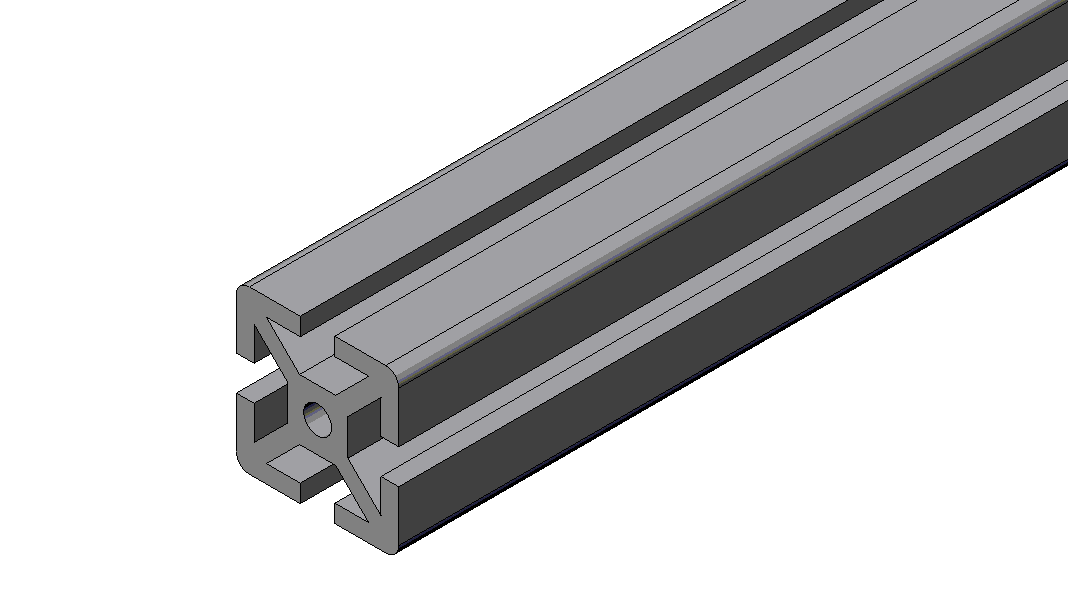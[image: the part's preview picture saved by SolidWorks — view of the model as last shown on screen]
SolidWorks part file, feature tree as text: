
SOLIDWORKS PART (.sldprt)
format: sldprt  version: not decoded by parser v0  size: 2,478,592 bytes
history: native  units: mm
features: sketch x48, cut_extrude x47, material x1 (+38 scaffold rows collapsed; 12 parser-record rows omitted)
feature tree (146):
  scaffold x38  (default folders/planes/origin — collapsed)
  material  "Material <not specified>"
  parser-record x12  (decoder bookkeeping rows leaked as tree rows — omitted from the tree; the rows remain in map.json)
  sketch  "Sketch1"  dims[c1.D2=3.048mm c1.D5=1.016mm c1.D6=1.016mm c1.D13=~1.042776mm c1.D15=6.5278mm c1.D3=5.08mm c1.D1=~17.549308mm c2.D1=45.0deg c2.D3=4.826mm c2.D4=4.826mm c2.D7=7.62mm c2.D8=7.62mm c2.D9=19.05mm c2.D10=12.7mm c2.D11=~7.529984mm c3.D11=2.0deg c3.D12=~36.763158mm c4.D12=3.0deg c5.D12=~36.763158mm c6.D12=2.0deg c6.D14=3.302mm c6.D10=19.05mm c6.D3=4.826mm c6.D5=4.064mm c6.D6=3.2385mm c6.D7=3.2385mm c6.D8=7.7724mm c6.D11=7.7724mm c7.D3=11.938mm c7.D4=11.938mm c7.D6=14.986mm c7.D7=9.4742mm]
  cut_extrude  "FinalCut"  Depth=609.6mm CutLength=609.6mm
  sketch  "Sketch38"
  sketch  "Sketch3"  dims[D1=20.6248mm D2=21.717mm]
  cut_extrude  "AFA1"  Depth=16.51mm
  sketch  "Sketch5"  dims[D1=20.6248mm D2=21.717mm]
  cut_extrude  "AFA2"  Depth=16.51mm
  sketch  "Sketch6"  dims[c1.D1=20.6248mm c1.D2=20.6248mm c2.D1=21.717mm]
  cut_extrude  "AFA3"  Depth=16.51mm
  sketch  "Sketch8"  dims[D2=20.6248mm D1=21.717mm]
  cut_extrude  "AFA4"  Depth=16.51mm
  sketch  "Sketch9"  dims[D2=20.6248mm D1=21.717mm]
  cut_extrude  "AFB1"  Depth=16.51mm
  sketch  "Sketch12"  dims[D2=20.6248mm D1=21.717mm]
  cut_extrude  "AFB2"  Depth=16.51mm
  sketch  "Sketch13"  dims[D3=20.6248mm D1=0.0mm D2=21.717mm]
  cut_extrude  "AFB3"  Depth=16.51mm
  sketch  "Sketch14"  dims[D2=20.6248mm D1=21.717mm]
  cut_extrude  "AFB4"  Depth=16.51mm
  sketch  "Sketch25"  dims[D1=20.6248mm D2=18.3134mm]
  cut_extrude  "BFA1"  Depth=16.51mm
  sketch  "Sketch27"  dims[D1=20.6248mm D2=18.3134mm]
  cut_extrude  "BFA2"  Depth=16.51mm
  sketch  "Sketch24"  dims[c1.D1=20.6248mm c1.D2=20.6248mm c2.D1=18.3134mm]
  cut_extrude  "BFA3"  Depth=16.51mm
  sketch  "Sketch23"  dims[c1.D1=20.6248mm c1.D2=20.6248mm c2.D1=18.3134mm]
  cut_extrude  "BFA4"  Depth=16.51mm
  sketch  "Sketch15"  dims[D2=20.6248mm D1=18.3134mm]
  cut_extrude  "BFB1"  Depth=16.51mm
  sketch  "Sketch17"  dims[D2=20.6248mm D1=18.3134mm]
  cut_extrude  "BFB2"  Depth=16.51mm
  sketch  "Sketch18"  dims[D2=20.6248mm D1=18.3134mm]
  cut_extrude  "BFB3"  Depth=16.51mm
  sketch  "Sketch19"  dims[D2=20.6248mm D1=18.3134mm]
  cut_extrude  "BFB4"  Depth=16.51mm
  sketch  "Sketch28"  dims[D1=7.62mm]
  cut_extrude  "TPA660015"  Depth=25.4mm
  sketch  "Sketch29"  dims[D1=7.62mm]
  cut_extrude  "TPB660015"  Depth=25.4mm
  sketch  "Sketch30"  dims[D1=7.874mm]
  cut_extrude  "TPA660034"  Depth=24.13mm
  sketch  "Sketch31"  dims[D1=7.874mm]
  cut_extrude  "TPB660034"  Depth=24.13mm
  sketch  "Sketch32"  dims[D1=8.128mm]
  cut_extrude  "TPA660033"  Depth=22.86mm
  sketch  "Sketch33"  dims[D1=8.128mm]
  cut_extrude  "TPB660033"  Depth=22.86mm
  sketch  "Sketch34"  dims[D1=9.525mm]
  cut_extrude  "TPA660009"  Depth=21.59mm
  sketch  "Sketch35"  dims[D1=9.525mm]
  cut_extrude  "TPB660009"  Depth=21.59mm
  sketch  "Sketch36"  dims[D1=11.1252mm]
  cut_extrude  "TPA660030"  Depth=20.32mm
  sketch  "Sketch37"  dims[D1=11.1252mm]
  cut_extrude  "TPB660030"  Depth=20.32mm
  sketch  "Sketch39"  dims[c1.D1=~44.828128mm c2.D1=45.0deg]
  cut_extrude  "MITA1"  [1 undecoded]
  sketch  "Sketch43"  dims[D2=19.05mm D1=28.575mm]
  cut_extrude  "MITCBA1"  [1 undecoded]
  sketch  "Sketch44"  dims[D1=8.3312mm D2=28.575mm]
  cut_extrude  "MITDRA1"  [1 undecoded]
  sketch  "Sketch45"  dims[c1.D1=~6.16906mm c1.D2=9.525mm c2.D1=17.4752mm]
  cut_extrude  "MITEBA1"  [1 undecoded]
  sketch  "Sketch46"  dims[D1=4.1656mm D2=17.4752mm]
  cut_extrude  "MITEDA1"  [1 undecoded]
  sketch  "Sketch40"  dims[c1.D1=~45.408282mm c2.D1=45.0deg]
  cut_extrude  "MITB1"  [1 undecoded]
  sketch  "Sketch47"  dims[c1.D1=~15.883714mm c1.D2=19.05mm c2.D1=28.575mm]
  cut_extrude  "MITCBB1"  [1 undecoded]
  sketch  "Sketch48"  dims[c1.D1=~8.496948mm c1.D2=8.3312mm c2.D1=28.575mm]
  cut_extrude  "MITDRB1"  [1 undecoded]
  sketch  "Sketch49"  dims[D2=9.525mm D1=17.4752mm]
  cut_extrude  "MITEBB1"  [1 undecoded]
  sketch  "Sketch50"  dims[D2=4.1656mm D1=17.4752mm]
  cut_extrude  "MITEDB1"  [1 undecoded]
  sketch  "Sketch41"  dims[c1.D1=~44.519605mm c2.D1=45.0deg]
  cut_extrude  "MITA3"  [1 undecoded]
  sketch  "Sketch51"  dims[D1=19.05mm D2=28.575mm]
  cut_extrude  "MITCBA3"  [1 undecoded]
  sketch  "Sketch52"  dims[c1.D1=~10.456475mm c1.D2=8.3312mm c2.D1=28.575mm]
  cut_extrude  "MITDRA3"  [1 undecoded]
  sketch  "Sketch53"  dims[D1=9.525mm D2=17.4752mm]
  cut_extrude  "MITEBA3"  [1 undecoded]
  sketch  "Sketch54"  dims[D1=4.1656mm D2=17.4752mm]
  cut_extrude  "MITEDA3"  [1 undecoded]
  sketch  "Sketch42"  dims[c1.D1=~45.044821mm c2.D1=45.0deg]
  cut_extrude  "MITB3"  [1 undecoded]
  sketch  "Sketch55"  dims[D1=19.05mm D2=28.575mm]
  cut_extrude  "MITCBB3"  [1 undecoded]
  sketch  "Sketch56"  dims[c1.D1=~11.643541mm c1.D2=8.3312mm c2.D1=28.575mm]
  cut_extrude  "MITDRB3"  [1 undecoded]
  sketch  "Sketch57"  dims[c1.D1=~5.356854mm c1.D2=9.525mm c2.D1=17.4752mm]
  cut_extrude  "MITEBB3"  [1 undecoded]
  sketch  "Sketch58"  dims[c1.D1=~5.947864mm c1.D2=4.1656mm c2.D1=17.4752mm]
  cut_extrude  "MITEDB3"  [1 undecoded]
decode coverage: 74 of 95 modeling features carry decoded parameters
note: ~ marks probable driven/reference dimensions
note: 20 parameter values undecoded
summary: no parameter record found for 20 features
note: suppression state not decoded; provenance and decode notes live in map.json
